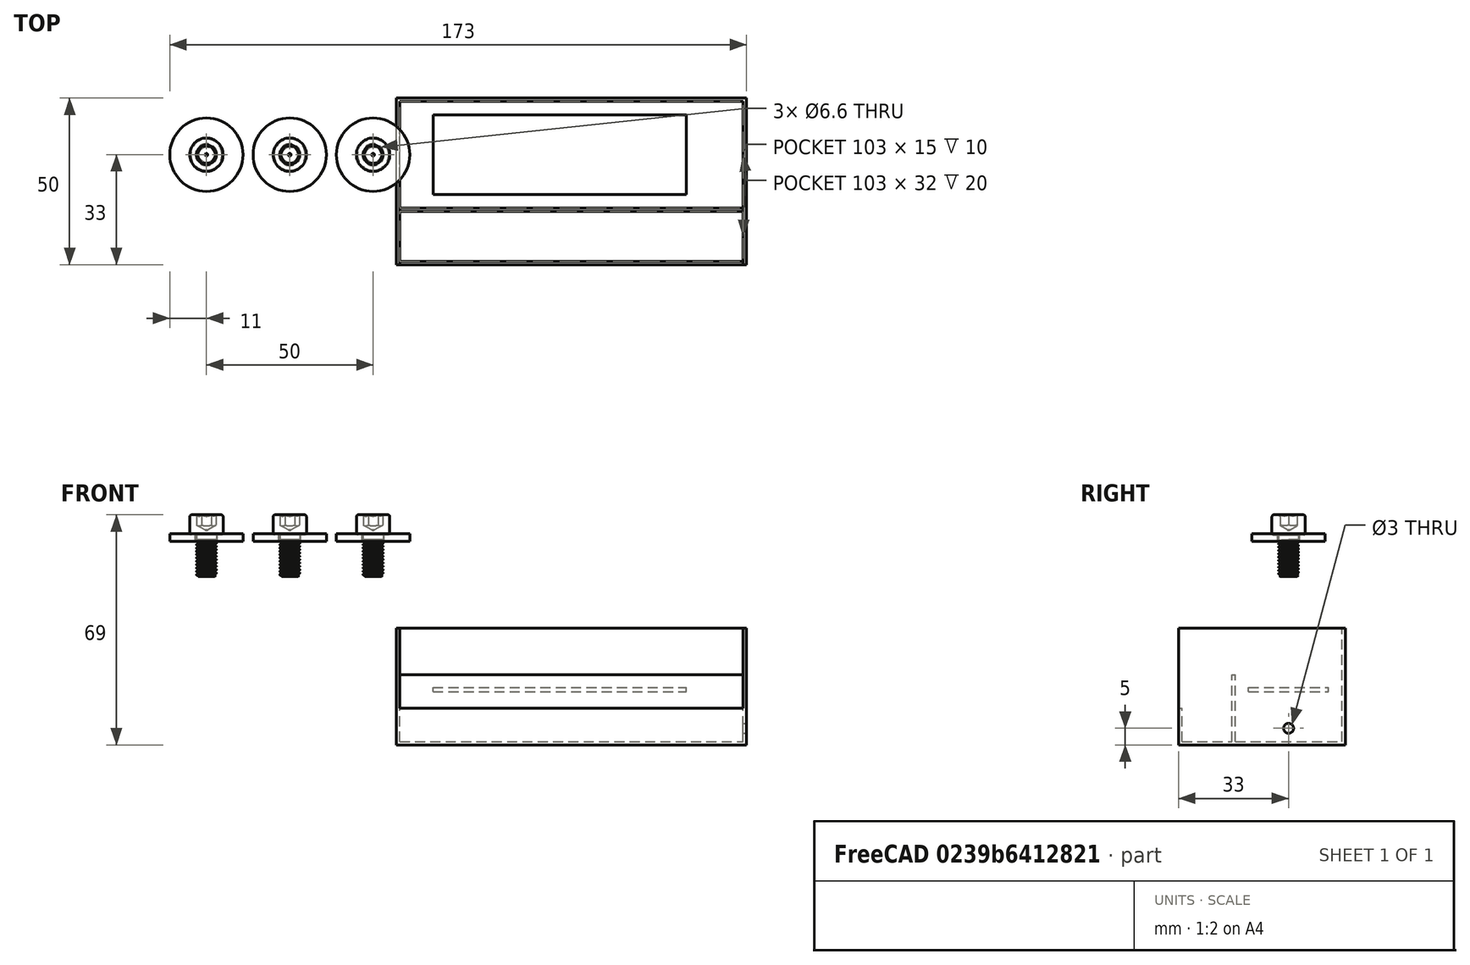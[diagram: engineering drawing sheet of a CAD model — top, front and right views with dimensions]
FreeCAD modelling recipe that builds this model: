
FCSTD DOCUMENT  (FreeCAD 0.19R24267 +99 (Git))
Label: infinityPoolSetup
License: All rights reserved
LicenseURL: http://en.wikipedia.org/wiki/All_rights_reserved
objects: Part::FeaturePython×6, Mesh::Feature×1, Part::Box×1, Part::Feature×1
note: 8 computed .brp shape members not serialized (recipe doc carries the construction recipe); baked Part::Feature solids carry a one-line shape summary decoded from their .brp

FEATURE [Mesh::Feature] poolSlideHolder_Sep2021
  Placement = pos=(82,45,10) rot=(0,0,1;3.14159rad)
FEATURE [Part::Box] Box004  label="Glass Slide"
  AttacherType = Attacher::AttachEngine3D
  Height = 1.2
  Length = 76
  Placement = pos=(13,21,16) rot=(0,0,1;0rad)
  Width = 24
FEATURE [Part::FeaturePython] Screw  label="M6x12-Screw"  # Fasteners workbench fastener (typed FeaturePython)
  Placement = pos=(-5,33,63) rot=(0,0,1;0rad)
  diameter = 7
  invert = false
  length = 14
  lengthCustom = 12
  matchOuter = false
  offset = 0
  thread = true
  type = 34
FEATURE [Part::FeaturePython] Washer001  label="M6-Washer"  # Fasteners workbench fastener (typed FeaturePython)
  Placement = pos=(-5,33,61) rot=(0,0,1;0rad)
  diameter = 2
  invert = false
  matchOuter = false
  offset = 0
  type = 7
FEATURE [Part::FeaturePython] Washer002  label="M6-Washer001"  # Fasteners workbench fastener (typed FeaturePython)
  Placement = pos=(-30,33,61) rot=(0,0,1;0rad)
  diameter = 2
  invert = false
  matchOuter = false
  offset = 0
  type = 7
FEATURE [Part::FeaturePython] Screw001  label="M6x12-Screw001"  # Fasteners workbench fastener (typed FeaturePython)
  Placement = pos=(-30,33,63) rot=(0,0,1;0rad)
  diameter = 7
  invert = false
  length = 14
  lengthCustom = 12
  matchOuter = false
  offset = 0
  thread = true
  type = 34
FEATURE [Part::FeaturePython] Washer003  label="M6-Washer002"  # Fasteners workbench fastener (typed FeaturePython)
  Placement = pos=(-55,33,61) rot=(0,0,1;0rad)
  diameter = 2
  invert = false
  matchOuter = false
  offset = 0
  type = 7
FEATURE [Part::FeaturePython] Screw002  label="M6x12-Screw002"  # Fasteners workbench fastener (typed FeaturePython)
  Placement = pos=(-55,33,63) rot=(0,0,1;0rad)
  diameter = 7
  invert = false
  length = 14
  lengthCustom = 12
  matchOuter = false
  offset = 0
  thread = true
  type = 34
FEATURE [Part::Feature] Solid006  label="infinityPool"
  Placement = pos=(2,0,0) rot=(0,0,1;0rad)
  shape: bbox 105 x 50 x 35 mm, 18 faces (baked)
